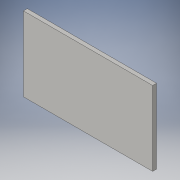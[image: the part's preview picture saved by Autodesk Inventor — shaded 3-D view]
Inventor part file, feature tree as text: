
AUTODESK INVENTOR PART (.ipt)
format: ipt  version: 2016 (Build 200138000, 138)  size: 90,112 bytes
history: native  units: in
note: dims shown in document units (in); Inventor stores cm internally (conversion verified against a paired STEP export)
features: extrude x1, sketch x1
ambient origin geometry x8: Origin, YZ Plane, XZ Plane, XY Plane, X Axis, Y Axis, Z Axis, Center Point
bodies: Solid1 (feature_tree)
feature tree (2):
  extrude  "Extrusion1"  Depth=0.5in TaperAngle=0.0deg
  sketch  "Sketch1"  dims[d0=16.5in d2=0.5in d3=0.0in]
